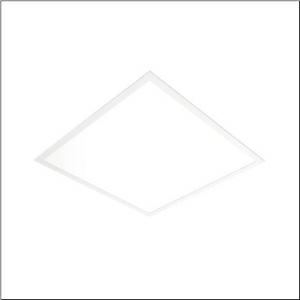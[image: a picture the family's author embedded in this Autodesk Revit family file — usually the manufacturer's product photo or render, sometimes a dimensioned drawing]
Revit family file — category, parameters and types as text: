
# Revit family: apollon_r__41_51mh11wd2422_5762
name_source: partatom
category: Lighting Fixtures
units: mm (PartAtom-declared; Revit-internal decimal feet)

## family parameters
Cut with Voids When Loaded = No
Host = Face
Light Source = No
Part Type = Normal
Room Calculation Point = No
Round Connector Dimension = Use Diameter
Shared = No

## types (1)
- Apollon® 41 (1 x LED, 3700 lm, 35 W, 4000K)
    Apparent Load = 35 VA
    CIE Flux Codes = 63 87 97 100 100
    Color Rendering = 80
    Color Temperature = 4000K
    Default Elevation = 1800 mm
    Description = Apollon® 41, office luminaire, primary optical cover: prismatic diffuser, of PS, light emission: direct distribution, primary light characteristic: symmetric, installation type: lay-in mounting, LED, rated luminous flux: 3.700lm, luminous efficacy: 105lm/W, light colour: 840, colour temperature: 4000K, control gear: ECG DALI, with terminal, 5-pole, mains connection: 220..240V, AC, 50/60Hz, rated input power: 35W, housing, of aluminium section, traffic white (RAL 9016), module: M625, length: 620mm, width: 620mm, height: 32mm, housing upper side, of sheet steel, protection rating (complete): IP20, protection rating (lamp compartment, on room side): IP40, insulation class (complete): insulation class II (safety insulation), certification: CE, ENEC, permissible operating ambient temperature: -20..+40°C, packaging unit: 1 piece
    Height = 0 mm  [stored 0 ft]
    Lamp = 1 x LED
    Lamp Light Flux = 3700 lm
    Lamp Power = 35 W
    Lamp count = 1
    Length = 622 mm
    Luminous efficacy = 106 lm/W
    Manufacturer = Siteco
    ModVariant = No
    Model = 51MH11WD2422
    Mounting Place = Ceiling
    Mounting Type = Recessed
    Number of Poles = 1
    OnlyDefault = Yes
    Power Factor = 1
    Product Name = Apollon® 41
    Product group = office luminaire | ceiling recessed
    ProductGroupID = 400
    Protection Class = Protection class II
    Protection Degree = IP 20
    RLX_Detail_Level = 1
    RlxData = <blob elided: 14877 chars, md5=afdc4b2a>
    Socket = socket
    Standby Power = 0 W
    System Light Flux = 3700 lm
    System Power = 35 W
    Type Comments = Product without accessories
    Type Image = l_1003755.jpg
    URL = http://relux.com
    VarID = ---
    Voltage = 0 V
    Weight = 0.00 kg
    Width = 622 mm

note: [stored X ft] marks values corroborated as IEEE doubles in the binary element streams (Revit-internal decimal feet)

## geometry (parser evidence)
native form markers: Sweep x11
no freeform markers — native parametric forms only
